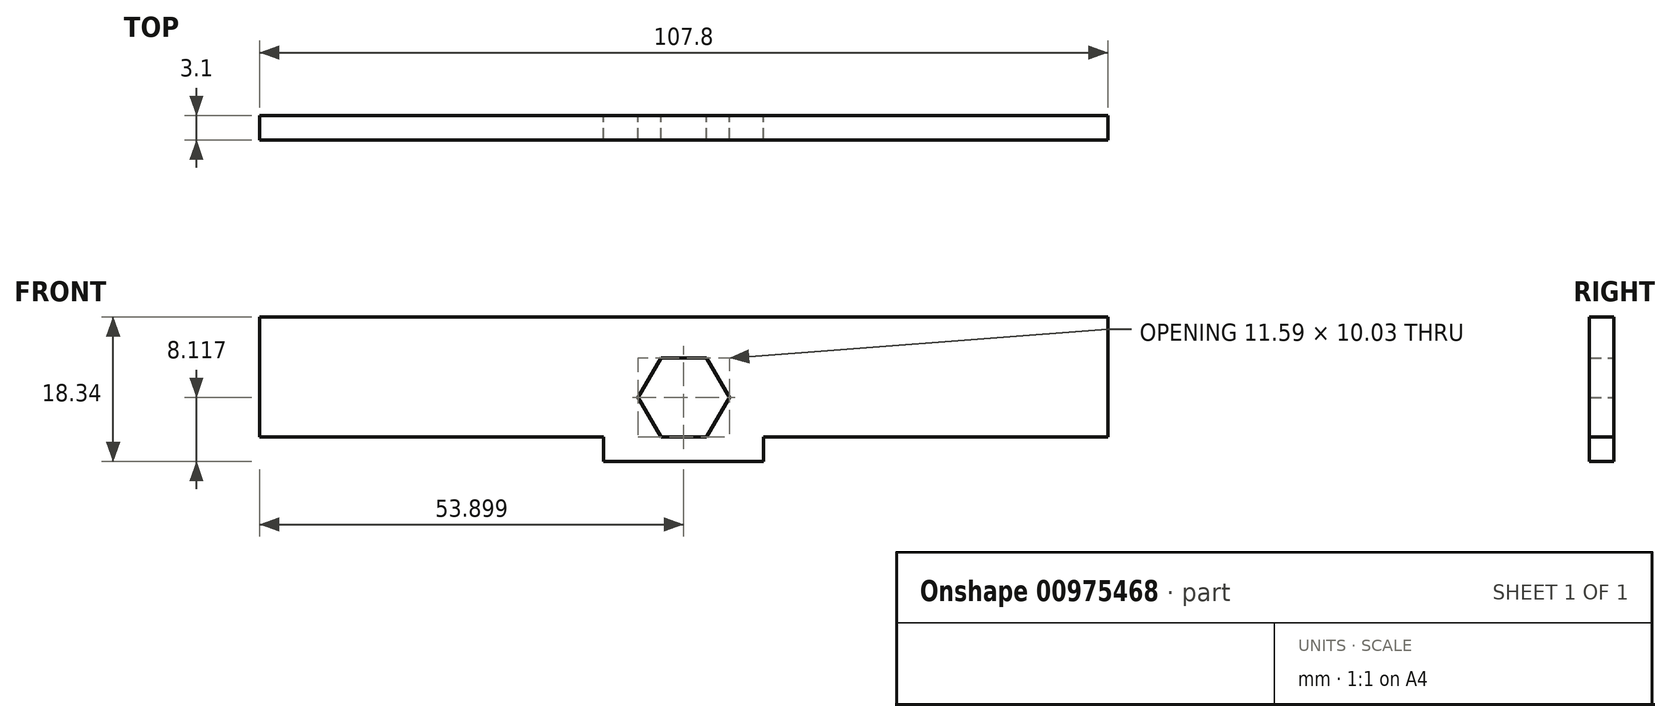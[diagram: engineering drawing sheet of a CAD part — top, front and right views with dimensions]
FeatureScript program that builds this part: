
annotation { "Feature Type Name" : "Feature", "Feature Type Description" : "" }
export const myFeature = defineFeature(function(context is Context, id is Id, definition is map)
    precondition{}
    {
        {
            var Q0;
            Q0=qCreatedBy(makeId("Front.planeOp"),FACE);
            var sketch = newSketch(context, id + "F0", { "sketchPlane" : qUnion([Q0])});
            skLineSegment(sketch, "E0.bottom", {"start": v(0, 0) * mm, "end": v(107.8, 0) * mm});
            skLineSegment(sketch, "E0.top", {"start": v(0, 15.24) * mm, "end": v(107.8, 15.24) * mm});
            skLineSegment(sketch, "E0.left", {"start": v(0, 0) * mm, "end": v(0, 15.24) * mm});
            skLineSegment(sketch, "E0.right", {"start": v(107.8, 0) * mm, "end": v(107.8, 15.24) * mm});
            skLineSegment(sketch, "E1.bottom", {"start": v(43.74, 0) * mm, "end": v(64.06, 0) * mm});
            skLineSegment(sketch, "E1.top", {"start": v(43.74, -3.1) * mm, "end": v(64.06, -3.1) * mm});
            skLineSegment(sketch, "E1.left", {"start": v(43.74, 0) * mm, "end": v(43.74, -3.1) * mm});
            skLineSegment(sketch, "E1.right", {"start": v(64.06, 0) * mm, "end": v(64.06, -3.1) * mm});
            skLineSegment(sketch, "E2", {"start": v(53.9, 15.24) * mm, "end": v(53.9, 0) * mm, "construction": true});
            skLineSegment(sketch, "E3", {"start": v(53.9, 0) * mm, "end": v(53.9, 3.07) * mm});
            skCircle(sketch, "E4.cCircle", {"center": v(53.9, 5.02) * mm, "radius": 5.02 * mm, "construction": true});
            skLineSegment(sketch, "E4.0", {"start": v(56.8, 10.03) * mm, "end": v(59.7, 5.02) * mm});
            skLineSegment(sketch, "E4.1", {"start": v(59.7, 5.02) * mm, "end": v(56.8, 0) * mm});
            skLineSegment(sketch, "E4.2", {"start": v(56.8, 0) * mm, "end": v(51, 0) * mm});
            skLineSegment(sketch, "E4.3", {"start": v(51, 0) * mm, "end": v(48.1, 5.02) * mm});
            skLineSegment(sketch, "E4.4", {"start": v(48.1, 5.02) * mm, "end": v(51, 10.03) * mm});
            skLineSegment(sketch, "E4.5", {"start": v(51, 10.03) * mm, "end": v(56.8, 10.03) * mm});
            skPoint(sketch, "E4.0.midPoint", {"position": v(58.24, 7.52) * mm});
            skSolve(sketch);
        }
        {
            var Q0;
            Q0=makeQuery(id+"F0.imprint","IMPRINT",FACE,{"disambiguationData":[TD([[makeQuery(id+"F0.imprint","IMPRINT",EDGE,{"derivedFrom":sQuery(id+"F0.wireOp",EDGE,"E0.top")}),-1.0]])]});
            var Q1;
            Q1=makeQuery(id+"F0.imprint","IMPRINT",FACE,{"disambiguationData":[TD([[makeQuery(id+"F0.imprint","IMPRINT",EDGE,{"derivedFrom":sQuery(id+"F0.wireOp",EDGE,"E1.top")}),1.0]])]});
            extrude(context, id + "F1", {"entities" : qUnion([Q0, Q1]), "depth" : 3.1 * mm, "offsetDistance" : 25.4 * mm});
        }
    });
